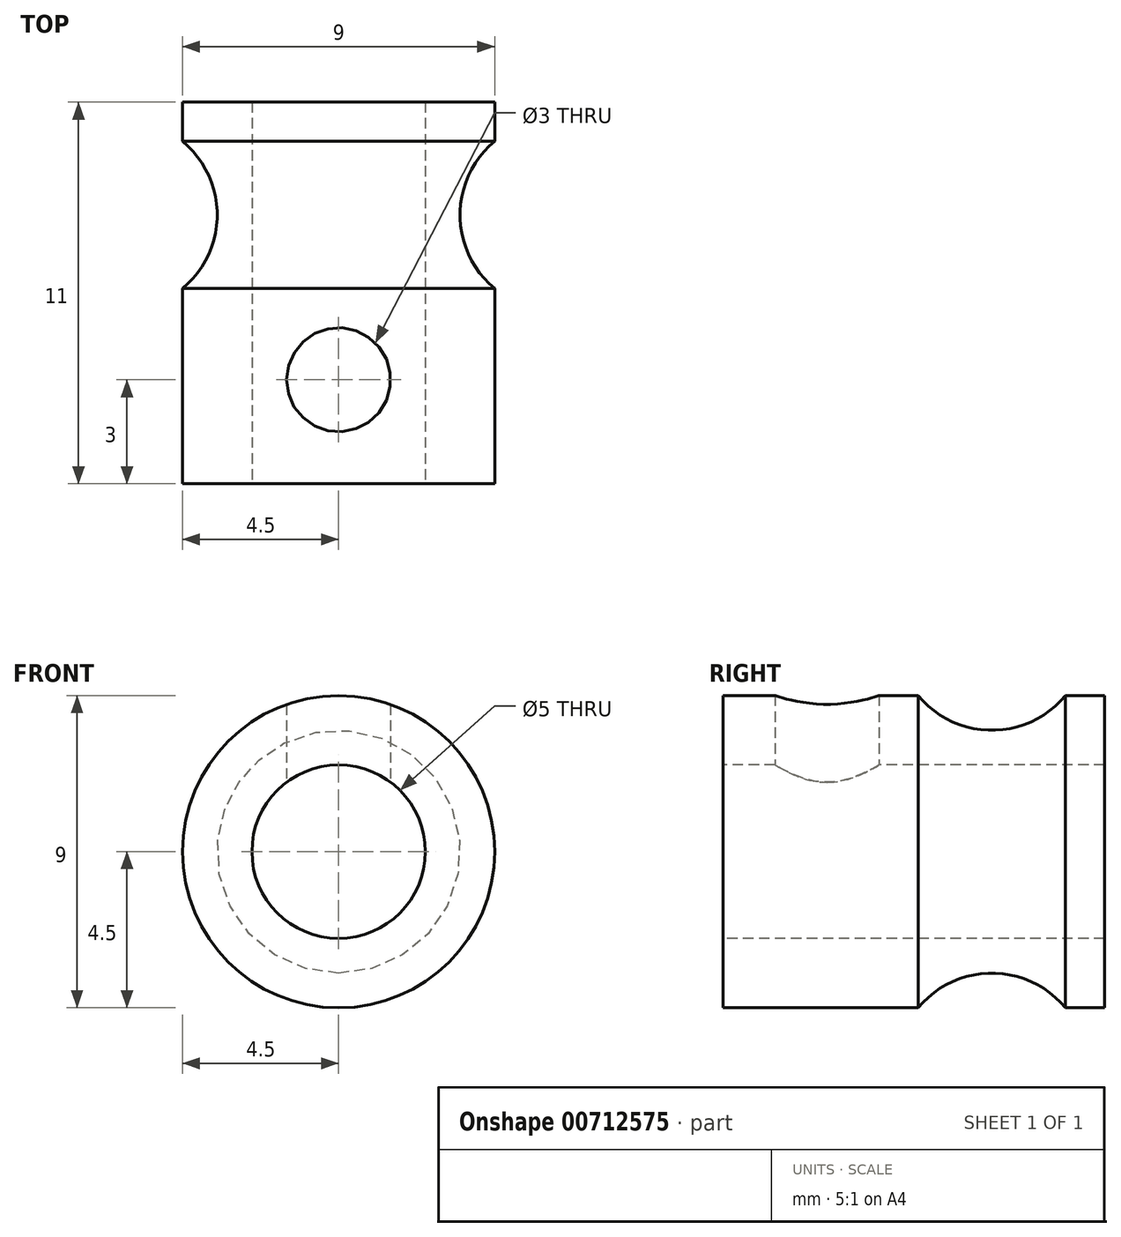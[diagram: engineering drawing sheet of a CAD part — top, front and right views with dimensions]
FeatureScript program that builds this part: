
annotation { "Feature Type Name" : "Feature", "Feature Type Description" : "" }
export const myFeature = defineFeature(function(context is Context, id is Id, definition is map)
    precondition{}
    {
        {
            var Q0;
            Q0=qCreatedBy(makeId("Top.planeOp"),FACE);
            var sketch = newSketch(context, id + "F0", { "sketchPlane" : qUnion([Q0])});
            skLineSegment(sketch, "E0", {"start": v(2.5, 0) * mm, "end": v(2.5, 11) * mm});
            skLineSegment(sketch, "E1", {"start": v(2.5, 11) * mm, "end": v(4.5, 11) * mm});
            skLineSegment(sketch, "E2", {"start": v(4.5, 11) * mm, "end": v(4.5, 9.87) * mm});
            skLineSegment(sketch, "E3", {"start": v(2.5, 0) * mm, "end": v(4.5, 0) * mm});
            skLineSegment(sketch, "E4", {"start": v(4.5, 0) * mm, "end": v(4.5, 5.62) * mm});
            skArc(sketch, "E5", {"start": v(4.5, 9.87) * mm, "mid": v(3.5, 7.75) * mm, "end": v(4.5, 5.62) * mm});
            skLineSegment(sketch, "E6", {"start": v(0, 0) * mm, "end": v(0, 11) * mm, "construction": true});
            skLineSegment(sketch, "E7.0", {"start": v(3.5, 0) * mm, "end": v(3.5, 11) * mm, "construction": true});
            skSolve(sketch);
        }
        {
            var Q0;
            Q0 = qSketchRegion(id + "F0", true);
            var Q1;
            Q1=sQuery(id+"F0.wireOp",EDGE,"E6");
            revolve(context, id + "F1", {"surfaceOperationType" : NewSurfaceOperationType.NEW, "entities" : qUnion([Q0]), "axis" : qUnion([Q1]), "revolveType" : RevolveType.FULL});
        }
        {
            var Q0;
            Q0=qCreatedBy(makeId("Top.planeOp"),FACE);
            var sketch = newSketch(context, id + "F2", { "sketchPlane" : qUnion([Q0])});
            skCircle(sketch, "E8", {"center": v(0, 3) * mm, "radius": 1.5 * mm});
            skSolve(sketch);
        }
        {
            var Q0;
            Q0=makeQuery(id+"F2.imprint","IMPRINT",FACE,{"disambiguationData":[TD([[makeQuery(id+"F2.imprint","IMPRINT",EDGE,{"derivedFrom":sQuery(id+"F2.wireOp",EDGE,"E8")}),1.0]])]});
            extrude(context, id + "F3", {"entities" : qUnion([Q0]), "operationType" : NewBodyOperationType.REMOVE, "endBound" : BoundingType.THROUGH_ALL, "depth" : 25 * mm, "offsetDistance" : 25 * mm});
        }
    });
